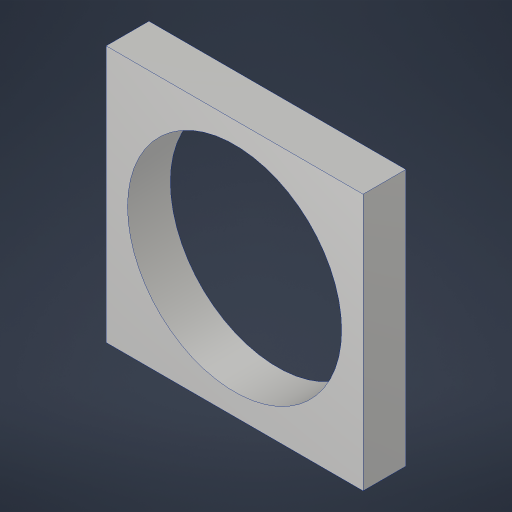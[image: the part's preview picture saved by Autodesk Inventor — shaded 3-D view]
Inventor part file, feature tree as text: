
AUTODESK INVENTOR PART (.ipt)
format: ipt  version: 2023.4 (Build 274418000, 418)  size: 179,712 bytes
history: native  units: in
note: dims shown in document units (in); Inventor stores cm internally (conversion verified against a paired STEP export)
features: extrude x2, sketch x1
ambient origin geometry x8: Origin, YZ Plane, XZ Plane, XY Plane, X Axis, Y Axis, Z Axis, Center Point
bodies: Solid1 (feature_tree)
feature tree (3):
  extrude  "Extrusion1"  Depth=1.875in
  extrude  "Extrusion2"  TaperAngle=0.0deg  [1 undecoded]
  sketch  "Sketch2"  dims[d3=0.0in d4=1.875in d5=0.0in d6=0.0in]
note: 1 required parameter value undecoded (feature->parameter linkage not recoverable at this tier; creation-order binding heuristic only, values carry confidence <= 0.55)
